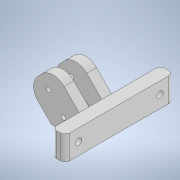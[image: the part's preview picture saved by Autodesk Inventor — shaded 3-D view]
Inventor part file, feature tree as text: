
AUTODESK INVENTOR PART (.ipt)
format: ipt  version: 2022 (Build 260153000, 153)  size: 240,640 bytes
history: native  units: in
note: dims shown in document units (in); Inventor stores cm internally (conversion verified against a paired STEP export)
features: plane x4, sketch x4, projected_geometry x4, hole x2, mirror x2, extrude x1, fillet x1
ambient origin geometry x8: Origin, YZ Plane, XZ Plane, XY Plane, X Axis, Y Axis, Z Axis, Center Point
bodies: Body1 (feature_tree)
feature tree (18):
  plane  "Work Plane1"
  hole  "Hole1"  [1 undecoded]
  extrude  "Extrusion4"  Depth=0.1575in
  plane  "Work Plane2"
  mirror  "Mirror1"
  fillet  "Fillet1"  Radius=0.3543in
  hole  "Hole5"  [1 undecoded]
  plane  "Work Plane3"
  mirror  "Mirror2"
  sketch  "Sketch1"  dims[d0=-0.2559in d1=0.5118in d2=0.0in]
  sketch  "Sketch3"  dims[d5=0.0996in d6=0.2362in d7=0.1575in d8=0.0787in d9=90.0deg d10=0.315in d11=0.8108in]
  sketch  "Sketch5"  dims[d19=0.0996in d20=0.2362in d21=0.1575in d22=0.0787in d23=90.0deg d24=0.315in d25=0.8108in d26=0.3543in d27=0.3543in]
  projected_geometry  "Projected Loop1"
  sketch  "Sketch8"  dims[d28=0.0787in d29=0.0787in d30=0.0394in d31=0.3937in d32=0.0in d35=0.2756in d36=0.2756in d38=0.2067in d39=0.5748in d40=0.3287in d41=0.1417in d42=0.2362in d43=0.2559in d44=0.1181in d45=0.6181in d46=0.3937in d47=0.0in d48=0.1033in d49=0.1033in d50=0.938in d51=0.3346in d52=0.2559in d53=0.5906in]
  projected_geometry  "Projected Loop11"
  projected_geometry  "Projected Loop12"
  projected_geometry  "Projected Loop13"
  plane  "Work Plane4"
note: 2 required parameter values undecoded (feature->parameter linkage not recoverable at this tier; creation-order binding heuristic only, values carry confidence <= 0.55)
